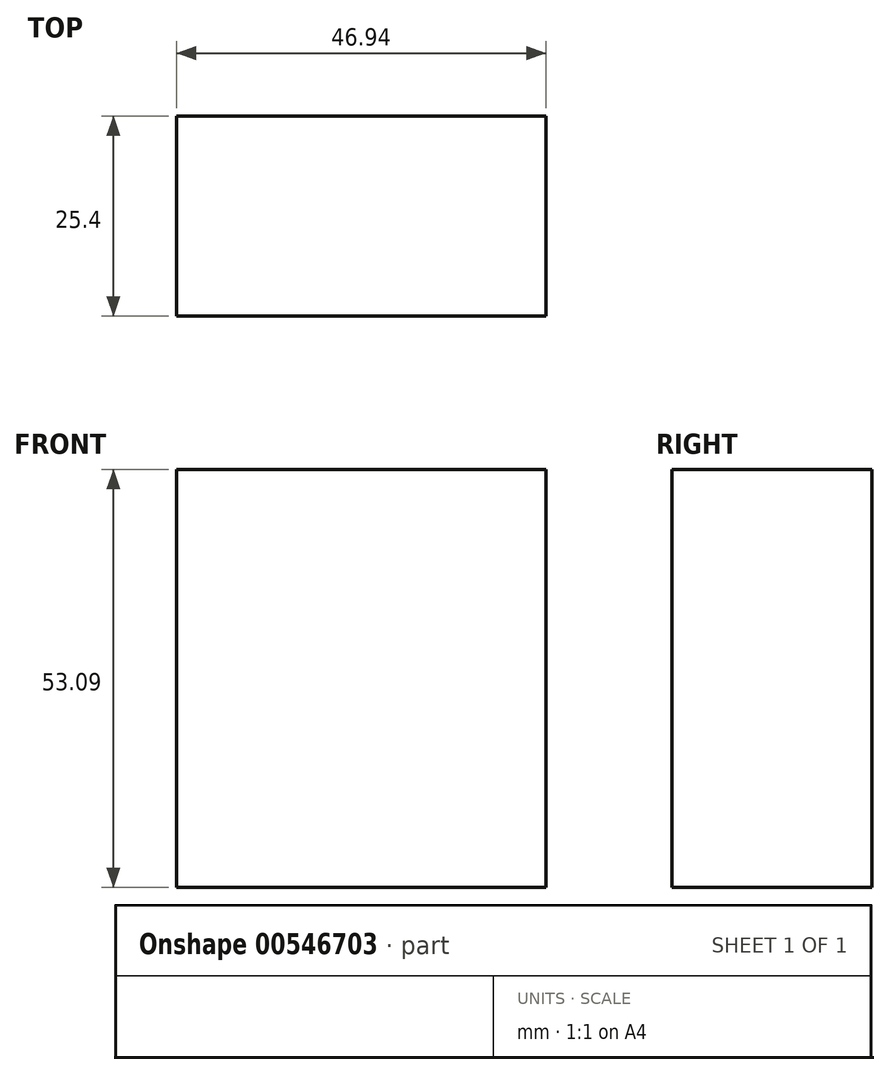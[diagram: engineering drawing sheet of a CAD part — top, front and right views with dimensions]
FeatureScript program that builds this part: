
annotation { "Feature Type Name" : "Feature", "Feature Type Description" : "" }
export const myFeature = defineFeature(function(context is Context, id is Id, definition is map)
    precondition{}
    {
        {
            var Q0;
            Q0=qCreatedBy(makeId("Front.planeOp"),FACE);
            var sketch = newSketch(context, id + "F0", { "sketchPlane" : qUnion([Q0])});
            skLineSegment(sketch, "E0.bottom", {"start": v(-93.27, 53.09) * mm, "end": v(-46.33, 53.09) * mm});
            skLineSegment(sketch, "E0.top", {"start": v(-93.27, 0) * mm, "end": v(-46.33, 0) * mm});
            skLineSegment(sketch, "E0.left", {"start": v(-93.27, 53.09) * mm, "end": v(-93.27, 0) * mm});
            skLineSegment(sketch, "E0.right", {"start": v(-46.33, 53.09) * mm, "end": v(-46.33, 0) * mm});
            skSolve(sketch);
        }
        {
            var Q0;
            Q0 = qSketchRegion(id + "F0", true);
            extrude(context, id + "F1", {"entities" : qUnion([Q0]), "depth" : 25.4 * mm, "offsetDistance" : 25.4 * mm});
        }
    });
